# Revit family: SANINDUSA_142410004_Winner_Bidet352x531x405_V0
name_source: partatom
category: Plumbing Fixtures
units: mm (PartAtom-declared; Revit-internal decimal feet)

## family parameters
Always vertical = Yes
Cut with Voids When Loaded = No
OmniClass Number = 23.45.00.00
OmniClass Title = Sanitary, Laundry, and Cleaning Equipment
Part Type = Normal
Room Calculation Point = No
Round Connector Dimension = Use Diameter
Shared = No
Work Plane-Based = No

## types (1)
- SANINDUSA_142410004_Winner_Bidet352x531x405_V0
    AssetType = Fixed
    BidetMounting = pedestal
    Category = Pr_40_20_06_11,Bidets
    CodePerformance = EN 14528:2007 - CL 25; EN 35:2014
    Color = white
    Constituents = 24 - fixing kit for bidet (included)
    Cost = 0 $
    Description = Waste water appliance for washing the excretory organs while sitting astride the bowl (BS6100)
    DrainSize = 45 mm  [stored 0.147638 ft]
    Edition number = 1
    Element Type = BIDET: Waste water appliance for washing the excretory organs while sitting astride the bowl
    Features = Domestic and hotel use. Easy to clean. With hole for one tap
    Finish = gloss
    Installation Instructions = https://www.tec.sanindusa.pt
    InstallationDate = 1900-12-31T23:59:59
    Manufacturer = Sanindusa
    ManufacturerName = Sanindusa
    ManufacturerURL = http://www.sanindusa.pt
    Material = Vitreous China
    Model = 142410004
    ModelNumber = 142410004
    ModelReference = Winner
    Name = Winner_bidet
    NominalDepth = 154 mm  [stored 0.505249 ft]
    NominalHeight = 405 mm
    NominalLength = 352 mm  [stored 1.15486 ft]
    NominalWidth = 531 mm  [stored 1.74213 ft]
    Pre-defined type (IFC) = BIDET
    ProductInformation = https://www.tec.sanindusa.pt
    ProductionYear = 2020
    Size = 352x531x405
    SpilloverLevel = 100
    Type (IFC) = IfcSanitaryTerminalType
    URL = www.sanindusa.pt
    Uniclass2015Code = Pr_40_20_06_18
    Uniclass2015Title = Bidets
    Version = 1
    WarrantyDescription = https://www.tec.sanindusa.pt
    WarrantyDurationParts = 5
    WarrantyDurationUnit = year
    WarrantyStartDate = 1900-12-31T23:59:59
    Weight = 22.70 kg

note: [stored X ft] marks values corroborated as IEEE doubles in the binary element streams (Revit-internal decimal feet)

## geometry (parser evidence)
native form markers: Sweep x6
no freeform markers — native parametric forms only
